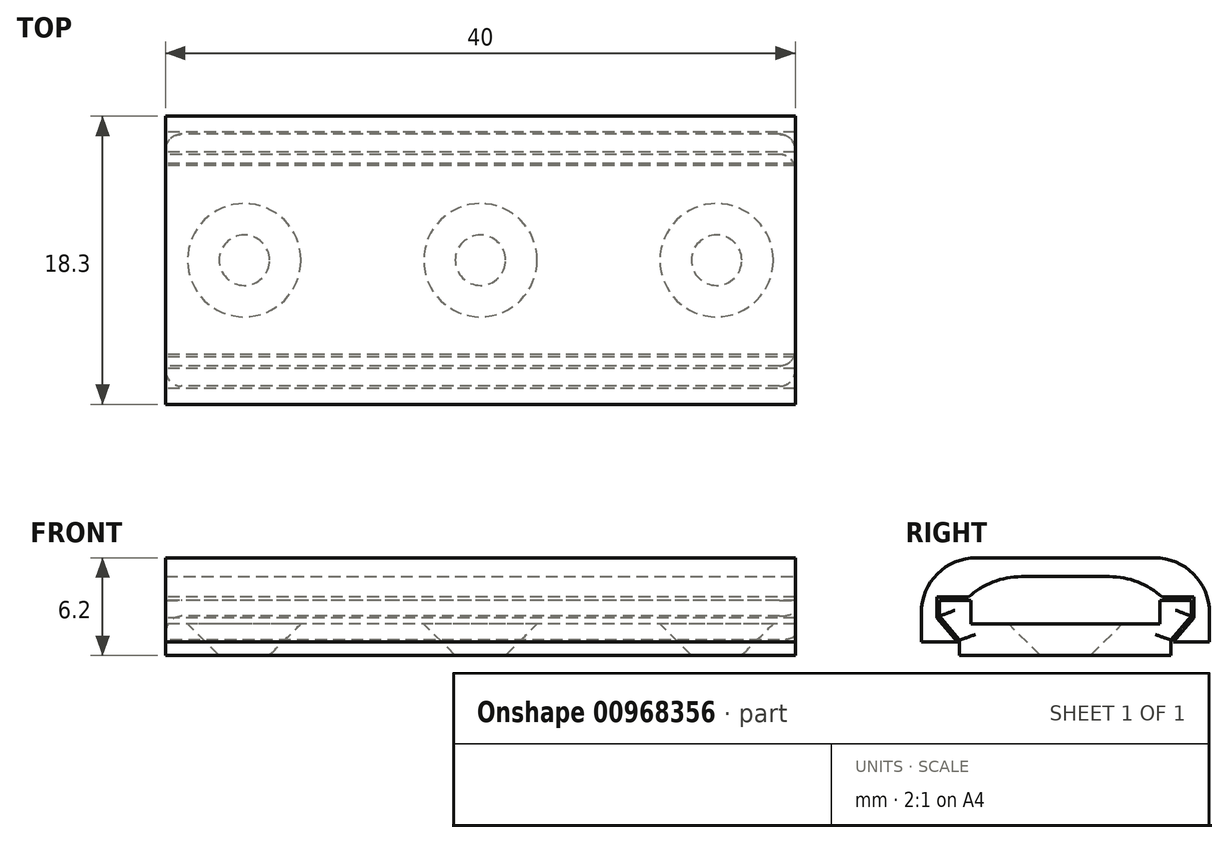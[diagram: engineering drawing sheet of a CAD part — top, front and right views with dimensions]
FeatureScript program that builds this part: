
annotation { "Feature Type Name" : "Feature", "Feature Type Description" : "" }
export const myFeature = defineFeature(function(context is Context, id is Id, definition is map)
    precondition{}
    {
        {
            assignVariable(context, id + "F0", {"name" : "lengt", "anyValue" : 40});
        }
        {
            var Q0;
            Q0=qCreatedBy(makeId("Top.planeOp"),FACE);
            var sketch = newSketch(context, id + "F1", { "sketchPlane" : qUnion([Q0])});
            skLineSegment(sketch, "E0.bottom", {"start": v(20, -6) * mm, "end": v(-20, -6) * mm});
            skLineSegment(sketch, "E0.top", {"start": v(20, 6) * mm, "end": v(-20, 6) * mm});
            skLineSegment(sketch, "E0.left", {"start": v(20, -6) * mm, "end": v(20, 6) * mm});
            skLineSegment(sketch, "E0.right", {"start": v(-20, -6) * mm, "end": v(-20, 6) * mm});
            skPoint(sketch, "E0.middle", {"position": v(0, 0) * mm});
            skLineSegment(sketch, "E1.0", {"start": v(20, 8) * mm, "end": v(-20, 8) * mm});
            skLineSegment(sketch, "E2.0", {"start": v(20, -8) * mm, "end": v(-20, -8) * mm});
            skLineSegment(sketch, "E3", {"start": v(-20, 6) * mm, "end": v(-20, 8) * mm});
            skLineSegment(sketch, "E4", {"start": v(20, 8) * mm, "end": v(20, 6) * mm});
            skLineSegment(sketch, "E5", {"start": v(20, -6) * mm, "end": v(20, -8) * mm});
            skLineSegment(sketch, "E6", {"start": v(-20, -6) * mm, "end": v(-20, -8) * mm});
            skCircle(sketch, "E7", {"center": v(0, 0) * mm, "radius": 1.6 * mm});
            skCircle(sketch, "E8", {"center": v(-15, 0) * mm, "radius": 1.6 * mm});
            skLineSegment(sketch, "E9", {"start": v(-20, 0) * mm, "end": v(-15, 0) * mm, "construction": true});
            skLineSegment(sketch, "E10", {"start": v(0, 8) * mm, "end": v(0, 14.17) * mm, "construction": true});
            skLineSegment(sketch, "E11.MirrorCS", {"start": v(20, 0) * mm, "end": v(15, 0) * mm, "construction": true});
            skCircle(sketch, "E12.MirrorC", {"center": v(15, 0) * mm, "radius": 1.6 * mm});
            skSolve(sketch);
        }
        {
            var Q0;
            Q0=makeQuery(id+"F1.imprint","IMPRINT",FACE,{"disambiguationData":[TD([[makeQuery(id+"F1.imprint","IMPRINT",EDGE,{"derivedFrom":sQuery(id+"F1.wireOp",EDGE,"E0.bottom")}),-1.0]])]});
            extrude(context, id + "F2", {"entities" : qUnion([Q0]), "depth" : 2 * mm, "offsetDistance" : 25 * mm});
        }
        {
            var Q0;
            Q0=makeQuery(id+"F1.imprint","IMPRINT",FACE,{"disambiguationData":[TD([[makeQuery(id+"F1.imprint","IMPRINT",EDGE,{"derivedFrom":sQuery(id+"F1.wireOp",EDGE,"E0.top")}),-1.0]])]});
            var Q1;
            Q1=makeQuery(id+"F1.imprint","IMPRINT",FACE,{"disambiguationData":[TD([[makeQuery(id+"F1.imprint","IMPRINT",EDGE,{"derivedFrom":sQuery(id+"F1.wireOp",EDGE,"E0.bottom")}),1.0]])]});
            extrude(context, id + "F3", {"entities" : qUnion([Q0, Q1]), "operationType" : NewBodyOperationType.ADD, "depth" : 3.5 * mm, "offsetDistance" : 25 * mm});
        }
        {
            var Q0;
            Q0=makeQuery(id+"F3.boolean.opBoolean","MERGE",FACE,{"derivedFrom":[makeQuery(id+"F2.opExtrude","SWEPT_FACE",FACE,{"disambiguationData":[OSD([sQuery(id+"F1.wireOp",EDGE,"E0.right")])]}),makeQuery(id+"F3.opExtrude","SWEPT_FACE",FACE,{"disambiguationData":[OSD([sQuery(id+"F1.wireOp",EDGE,"E3")])]}),makeQuery(id+"F3.opExtrude","SWEPT_FACE",FACE,{"disambiguationData":[OSD([sQuery(id+"F1.wireOp",EDGE,"E6")])]})]});
            var sketch = newSketch(context, id + "F4", { "sketchPlane" : qUnion([Q0])});
            skLineSegment(sketch, "E13", {"start": v(-8, 3.5) * mm, "end": v(-8, 2.5) * mm});
            skLineSegment(sketch, "E14", {"start": v(-8, 2.5) * mm, "end": v(-6.71, 0.97) * mm});
            skLineSegment(sketch, "E15", {"start": v(-6.71, 0.97) * mm, "end": v(-6.71, 0) * mm});
            skLineSegment(sketch, "E16", {"start": v(-6.71, 0.97) * mm, "end": v(-6.96, 0.97) * mm, "construction": true});
            skLineSegment(sketch, "E17", {"start": v(0, 0) * mm, "end": v(0, 2) * mm, "construction": true});
            skLineSegment(sketch, "E18.MirrorCS", {"start": v(6.71, 0.97) * mm, "end": v(6.71, 0) * mm});
            skLineSegment(sketch, "E19.MirrorCS", {"start": v(8, 2.5) * mm, "end": v(6.71, 0.97) * mm});
            skSolve(sketch);
        }
        {
            var Q0;
            {var subQ0=sQuery(id+"F4.wireOp",EDGE,"E14");Q0=makeQuery(id+"F4.imprint","IMPRINT",FACE,{"disambiguationData":[TD([[makeQuery(id+"F4.imprint","IMPRINT",EDGE,{"derivedFrom":subQ0}),-1.0]])]});}
            var Q1;
            {var subQ0=sQuery(id+"F4.wireOp",EDGE,"E18.MirrorCS");Q1=makeQuery(id+"F4.imprint","IMPRINT",FACE,{"disambiguationData":[TD([[makeQuery(id+"F4.imprint","IMPRINT",EDGE,{"derivedFrom":subQ0}),1.0]])]});}
            extrude(context, id + "F5", {"entities" : qUnion([Q0, Q1]), "operationType" : NewBodyOperationType.REMOVE, "oppositeDirection" : true, "depth" : 282.2 * mm, "offsetDistance" : 25 * mm});
        }
        {
            var Q0;
            Q0=makeQuery(id+"F3.boolean.opBoolean","MERGE",FACE,{"derivedFrom":[makeQuery(id+"F2.opExtrude","SWEPT_FACE",FACE,{"disambiguationData":[OSD([sQuery(id+"F1.wireOp",EDGE,"E0.right")])]}),makeQuery(id+"F3.opExtrude","SWEPT_FACE",FACE,{"disambiguationData":[OSD([sQuery(id+"F1.wireOp",EDGE,"E3")])]}),makeQuery(id+"F3.opExtrude","SWEPT_FACE",FACE,{"disambiguationData":[OSD([sQuery(id+"F1.wireOp",EDGE,"E6")])]})]});
            var sketch = newSketch(context, id + "F6", { "sketchPlane" : qUnion([Q0])});
            skLineSegment(sketch, "E20.0", {"start": v(-8.15, 2.37) * mm, "end": v(-6.87, 0.84) * mm});
            skLineSegment(sketch, "E21", {"start": v(-8.15, 2.37) * mm, "end": v(-8.15, 5) * mm});
            skLineSegment(sketch, "E22", {"start": v(-6.87, 0.84) * mm, "end": v(-9.15, 0.84) * mm});
            skLineSegment(sketch, "E23", {"start": v(-9.15, 0.84) * mm, "end": v(-9.15, 6.2) * mm});
            skLineSegment(sketch, "E24", {"start": v(0, 0) * mm, "end": v(0, 2) * mm, "construction": true});
            skLineSegment(sketch, "E25", {"start": v(0, 2) * mm, "end": v(0, 9.07) * mm, "construction": true});
            skLineSegment(sketch, "E26", {"start": v(-8.15, 5) * mm, "end": v(0, 5) * mm});
            skLineSegment(sketch, "E27", {"start": v(-9.15, 6.2) * mm, "end": v(0, 6.2) * mm});
            skLineSegment(sketch, "E28.MirrorCS", {"start": v(6.87, 0.84) * mm, "end": v(9.15, 0.84) * mm});
            skLineSegment(sketch, "E29.MirrorCS", {"start": v(8.15, 2.37) * mm, "end": v(6.87, 0.84) * mm});
            skLineSegment(sketch, "E30.MirrorCS", {"start": v(8.15, 2.37) * mm, "end": v(8.15, 5) * mm});
            skLineSegment(sketch, "E31.MirrorCS", {"start": v(9.15, 0.84) * mm, "end": v(9.15, 6.2) * mm});
            skLineSegment(sketch, "E32.MirrorCS", {"start": v(8.15, 5) * mm, "end": v(0, 5) * mm});
            skLineSegment(sketch, "E33.MirrorCS", {"start": v(9.15, 6.2) * mm, "end": v(0, 6.2) * mm});
            skLineSegment(sketch, "E34", {"start": v(-8.15, 3.7) * mm, "end": v(-6.15, 3.7) * mm});
            skLineSegment(sketch, "E35", {"start": v(-6.15, 3.7) * mm, "end": v(-8.15, 6.08) * mm});
            skLineSegment(sketch, "E36", {"start": v(-8.15, 6.08) * mm, "end": v(-6.82, 6.08) * mm, "construction": true});
            skLineSegment(sketch, "E37.MirrorCS", {"start": v(6.15, 3.7) * mm, "end": v(8.15, 6.08) * mm});
            skLineSegment(sketch, "E38.MirrorCS", {"start": v(8.15, 3.7) * mm, "end": v(6.15, 3.7) * mm});
            skSolve(sketch);
        }
        {
            var Q0;
            Q0=makeQuery(id+"F6.imprint","IMPRINT",FACE,{"disambiguationData":[TD([[makeQuery(id+"F6.imprint","IMPRINT",EDGE,{"derivedFrom":sQuery(id+"F6.wireOp",EDGE,"E20.0")}),-1.0]])]});
            var Q1;
            {var subQ0=sQuery(id+"F6.wireOp",EDGE,"E34");Q1=makeQuery(id+"F6.imprint","IMPRINT",FACE,{"disambiguationData":[TD([[makeQuery(id+"F6.imprint","IMPRINT",EDGE,{"derivedFrom":subQ0}),1.0]])]});}
            var Q2;
            {var subQ0=sQuery(id+"F6.wireOp",EDGE,"E37.MirrorCS");Q2=makeQuery(id+"F6.imprint","IMPRINT",FACE,{"disambiguationData":[TD([[makeQuery(id+"F6.imprint","IMPRINT",EDGE,{"derivedFrom":subQ0}),-1.0]])]});}
            extrude(context, id + "F7", {"entities" : qUnion([Q0, Q1, Q2]), "oppositeDirection" : true, "depth" : (getVariable(context, 'lengt')) * mm, "offsetDistance" : 25 * mm});
        }
        {
            var Q0;
            Q0=makeQuery(id+"F3.opExtrude","SWEPT_EDGE",EDGE,{"disambiguationData":[OSD([sQuery(id+"F1.wireOp",EDGE,"E2.0"),sQuery(id+"F1.wireOp",EDGE,"E5")])]});
            var Q1;
            Q1=makeQuery(id+"F5.boolean.opBoolean","INTERSECT",EDGE,{"derivedFrom":[makeQuery(id+"F3.boolean.opBoolean","MERGE",FACE,{"derivedFrom":[makeQuery(id+"F2.opExtrude","SWEPT_FACE",FACE,{"disambiguationData":[OSD([sQuery(id+"F1.wireOp",EDGE,"E0.left")])]}),makeQuery(id+"F3.opExtrude","SWEPT_FACE",FACE,{"disambiguationData":[OSD([sQuery(id+"F1.wireOp",EDGE,"E4")])]}),makeQuery(id+"F3.opExtrude","SWEPT_FACE",FACE,{"disambiguationData":[OSD([sQuery(id+"F1.wireOp",EDGE,"E5")])]})]}),makeQuery(id+"F5.opExtrude","SWEPT_FACE",FACE,{"disambiguationData":[OSD([sQuery(id+"F4.wireOp",EDGE,"E18.MirrorCS")])]})]});
            var Q2;
            Q2=makeQuery(id+"F5.boolean.opBoolean","INTERSECT",EDGE,{"derivedFrom":[makeQuery(id+"F3.boolean.opBoolean","MERGE",FACE,{"derivedFrom":[makeQuery(id+"F2.opExtrude","SWEPT_FACE",FACE,{"disambiguationData":[OSD([sQuery(id+"F1.wireOp",EDGE,"E0.left")])]}),makeQuery(id+"F3.opExtrude","SWEPT_FACE",FACE,{"disambiguationData":[OSD([sQuery(id+"F1.wireOp",EDGE,"E4")])]}),makeQuery(id+"F3.opExtrude","SWEPT_FACE",FACE,{"disambiguationData":[OSD([sQuery(id+"F1.wireOp",EDGE,"E5")])]})]}),makeQuery(id+"F5.opExtrude","SWEPT_FACE",FACE,{"disambiguationData":[OSD([sQuery(id+"F4.wireOp",EDGE,"E19.MirrorCS")])]})]});
            var Q3;
            Q3=makeQuery(id+"F3.opExtrude","SWEPT_EDGE",EDGE,{"disambiguationData":[OSD([sQuery(id+"F1.wireOp",EDGE,"E1.0"),sQuery(id+"F1.wireOp",EDGE,"E4")])]});
            var Q4;
            Q4=makeQuery(id+"F5.boolean.opBoolean","INTERSECT",EDGE,{"derivedFrom":[makeQuery(id+"F3.boolean.opBoolean","MERGE",FACE,{"derivedFrom":[makeQuery(id+"F2.opExtrude","SWEPT_FACE",FACE,{"disambiguationData":[OSD([sQuery(id+"F1.wireOp",EDGE,"E0.left")])]}),makeQuery(id+"F3.opExtrude","SWEPT_FACE",FACE,{"disambiguationData":[OSD([sQuery(id+"F1.wireOp",EDGE,"E4")])]}),makeQuery(id+"F3.opExtrude","SWEPT_FACE",FACE,{"disambiguationData":[OSD([sQuery(id+"F1.wireOp",EDGE,"E5")])]})]}),makeQuery(id+"F5.opExtrude","SWEPT_FACE",FACE,{"disambiguationData":[OSD([sQuery(id+"F4.wireOp",EDGE,"E14")])]})]});
            var Q5;
            Q5=makeQuery(id+"F5.boolean.opBoolean","INTERSECT",EDGE,{"derivedFrom":[makeQuery(id+"F3.boolean.opBoolean","MERGE",FACE,{"derivedFrom":[makeQuery(id+"F2.opExtrude","SWEPT_FACE",FACE,{"disambiguationData":[OSD([sQuery(id+"F1.wireOp",EDGE,"E0.left")])]}),makeQuery(id+"F3.opExtrude","SWEPT_FACE",FACE,{"disambiguationData":[OSD([sQuery(id+"F1.wireOp",EDGE,"E4")])]}),makeQuery(id+"F3.opExtrude","SWEPT_FACE",FACE,{"disambiguationData":[OSD([sQuery(id+"F1.wireOp",EDGE,"E5")])]})]}),makeQuery(id+"F5.opExtrude","SWEPT_FACE",FACE,{"disambiguationData":[OSD([sQuery(id+"F4.wireOp",EDGE,"E15")])]})]});
            var Q6;
            Q6=makeQuery(id+"F3.opExtrude","SWEPT_EDGE",EDGE,{"disambiguationData":[OSD([sQuery(id+"F1.wireOp",EDGE,"E1.0"),sQuery(id+"F1.wireOp",EDGE,"E3")])]});
            var Q7;
            Q7=makeQuery(id+"F5.boolean.opBoolean","COPY",EDGE,{"derivedFrom":makeQuery(id+"F5.opExtrude","CAP_EDGE",EDGE,{"disambiguationData":[OSD([sQuery(id+"F4.wireOp",EDGE,"E14")])],"isStart":true})});
            var Q8;
            Q8=makeQuery(id+"F5.boolean.opBoolean","COPY",EDGE,{"derivedFrom":makeQuery(id+"F5.opExtrude","CAP_EDGE",EDGE,{"disambiguationData":[OSD([sQuery(id+"F4.wireOp",EDGE,"E15")])],"isStart":true})});
            var Q9;
            Q9=makeQuery(id+"F5.boolean.opBoolean","COPY",EDGE,{"derivedFrom":makeQuery(id+"F5.opExtrude","CAP_EDGE",EDGE,{"disambiguationData":[OSD([sQuery(id+"F4.wireOp",EDGE,"E19.MirrorCS")])],"isStart":true})});
            var Q10;
            Q10=makeQuery(id+"F5.boolean.opBoolean","COPY",EDGE,{"derivedFrom":makeQuery(id+"F5.opExtrude","CAP_EDGE",EDGE,{"disambiguationData":[OSD([sQuery(id+"F4.wireOp",EDGE,"E18.MirrorCS")])],"isStart":true})});
            var Q11;
            Q11=makeQuery(id+"F3.opExtrude","SWEPT_EDGE",EDGE,{"disambiguationData":[OSD([sQuery(id+"F1.wireOp",EDGE,"E2.0"),sQuery(id+"F1.wireOp",EDGE,"E6")])]});
            fillet(context, id + "F8", {"entities" : qUnion([Q0, Q1, Q2, Q3, Q4, Q5, Q6, Q7, Q8, Q9, Q10, Q11]), "radius" : 1 * mm, "tangentPropagation" : true, "allowEdgeOverflow" : false});
        }
        {
            var Q0;
            Q0=makeQuery(id+"F2.opExtrude","CAP_EDGE",EDGE,{"disambiguationData":[OSD([sQuery(id+"F1.wireOp",EDGE,"E8")])],"isStart":false});
            var Q1;
            Q1=makeQuery(id+"F2.opExtrude","CAP_EDGE",EDGE,{"disambiguationData":[OSD([sQuery(id+"F1.wireOp",EDGE,"E7")])],"isStart":false});
            var Q2;
            Q2=makeQuery(id+"F2.opExtrude","CAP_EDGE",EDGE,{"disambiguationData":[OSD([sQuery(id+"F1.wireOp",EDGE,"E12.MirrorC")])],"isStart":false});
            chamfer(context, id + "F9", {"entities" : qUnion([Q0, Q1, Q2]), "width" : 2 * mm, "tangentPropagation" : true});
        }
        {
            var Q0;
            Q0=makeQuery(id+"F7.opExtrude","SWEPT_EDGE",EDGE,{"disambiguationData":[OSD([sQuery(id+"F6.wireOp",EDGE,"E26"),sQuery(id+"F6.wireOp",EDGE,"E35")])]});
            var Q1;
            Q1=makeQuery(id+"F7.opExtrude","SWEPT_EDGE",EDGE,{"disambiguationData":[OSD([sQuery(id+"F6.wireOp",EDGE,"E32.MirrorCS"),sQuery(id+"F6.wireOp",EDGE,"E37.MirrorCS")])]});
            fillet(context, id + "F10", {"entities" : qUnion([Q0, Q1]), "radius" : 5 * mm, "tangentPropagation" : true, "allowEdgeOverflow" : false});
        }
        {
            var Q0;
            Q0=makeQuery(id+"F7.opExtrude","SWEPT_EDGE",EDGE,{"disambiguationData":[OSD([sQuery(id+"F6.wireOp",EDGE,"E31.MirrorCS"),sQuery(id+"F6.wireOp",EDGE,"E33.MirrorCS")])]});
            var Q1;
            Q1=makeQuery(id+"F7.opExtrude","SWEPT_EDGE",EDGE,{"disambiguationData":[OSD([sQuery(id+"F6.wireOp",EDGE,"E23"),sQuery(id+"F6.wireOp",EDGE,"E27")])]});
            fillet(context, id + "F11", {"entities" : qUnion([Q0, Q1]), "radius" : 3.5 * mm, "tangentPropagation" : true, "allowEdgeOverflow" : false});
        }
    });
